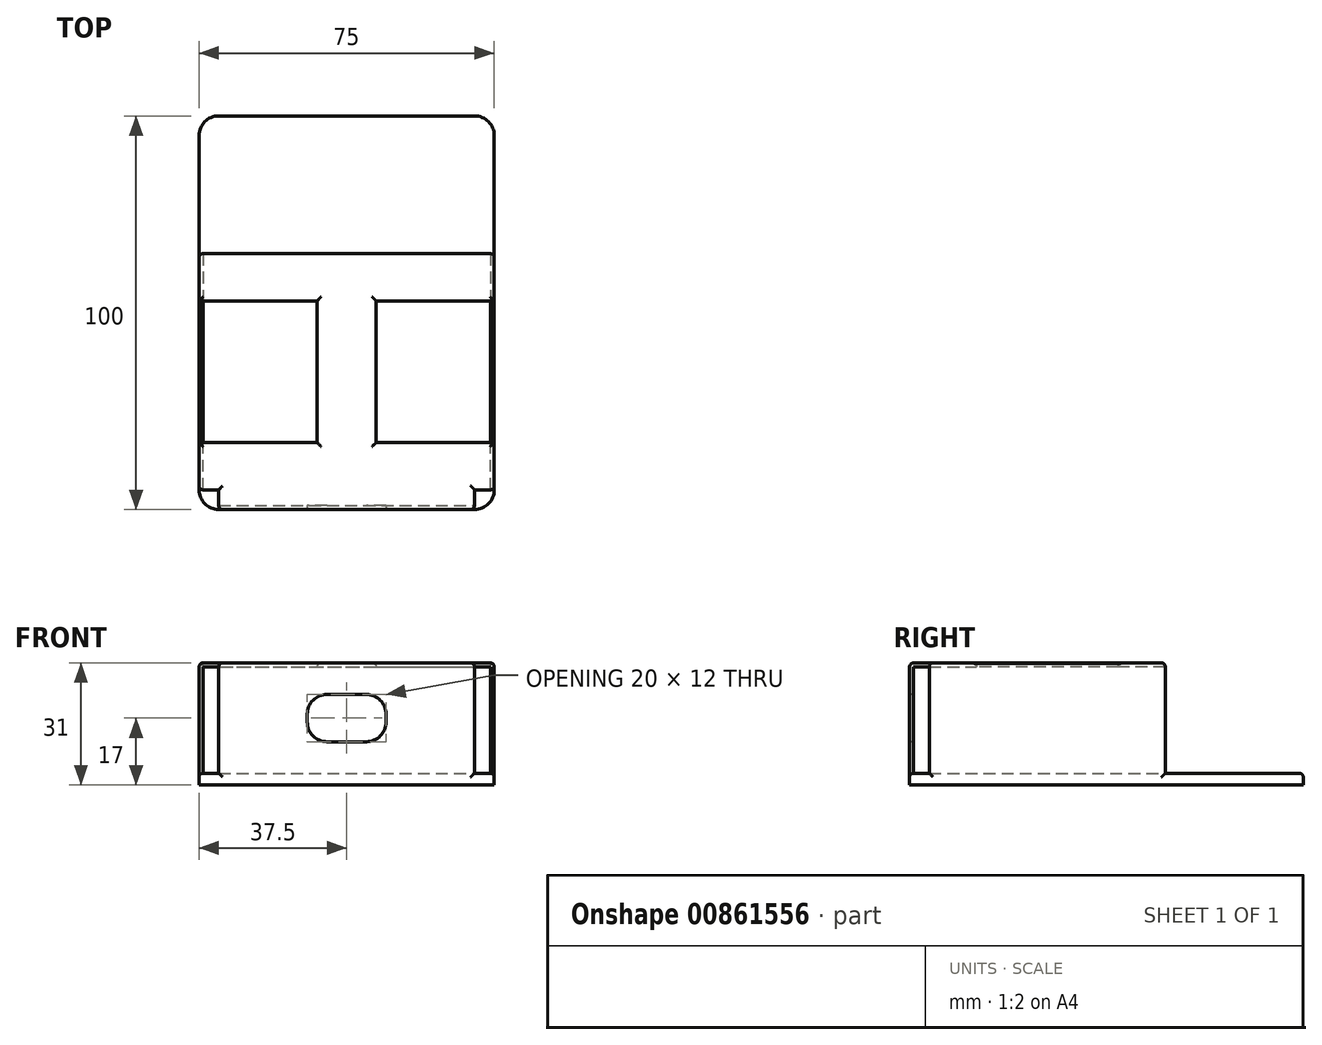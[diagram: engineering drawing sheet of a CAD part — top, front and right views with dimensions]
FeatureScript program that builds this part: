
annotation { "Feature Type Name" : "Feature", "Feature Type Description" : "" }
export const myFeature = defineFeature(function(context is Context, id is Id, definition is map)
    precondition{}
    {
        {
            var Q0;
            Q0=qCreatedBy(makeId("Top.planeOp"),FACE);
            var sketch = newSketch(context, id + "F0", { "sketchPlane" : qUnion([Q0])});
            skLineSegment(sketch, "E0.bottom", {"start": v(5, 0) * mm, "end": v(70, 0) * mm});
            skLineSegment(sketch, "E0.top", {"start": v(5, 100) * mm, "end": v(70, 100) * mm});
            skLineSegment(sketch, "E0.left", {"start": v(0, 5) * mm, "end": v(0, 95) * mm});
            skLineSegment(sketch, "E0.right", {"start": v(75, 5) * mm, "end": v(75, 95) * mm});
            skPoint(sketch, "E1.visualSharp", {"position": v(0, 100) * mm});
            skArc(sketch, "E1.filletArc", {"start": v(5, 100) * mm, "mid": v(1.46, 98.54) * mm, "end": v(0, 95) * mm});
            skPoint(sketch, "E2.visualSharp", {"position": v(75, 100) * mm});
            skArc(sketch, "E2.filletArc", {"start": v(75, 95) * mm, "mid": v(73.54, 98.54) * mm, "end": v(70, 100) * mm});
            skPoint(sketch, "E3.visualSharp", {"position": v(75, 0) * mm});
            skArc(sketch, "E3.filletArc", {"start": v(70, 0) * mm, "mid": v(73.54, 1.46) * mm, "end": v(75, 5) * mm});
            skPoint(sketch, "E4.visualSharp", {"position": v(0, 0) * mm});
            skArc(sketch, "E4.filletArc", {"start": v(0, 5) * mm, "mid": v(1.46, 1.46) * mm, "end": v(5, 0) * mm});
            skSolve(sketch);
        }
        {
            var Q0;
            Q0=makeQuery(id+"F0.imprint","IMPRINT",FACE,{"disambiguationData":[TD([[makeQuery(id+"F0.imprint","IMPRINT",EDGE,{"derivedFrom":sQuery(id+"F0.wireOp",EDGE,"E0.bottom")}),1.0]])]});
            extrude(context, id + "F1", {"entities" : qUnion([Q0]), "depth" : 3 * mm, "offsetDistance" : 25 * mm});
        }
        {
            var Q0;
            Q0=makeQuery(id+"F1.opExtrude","CAP_FACE",FACE,{"disambiguationData":[OSD([sQuery(id+"F0.wireOp",EDGE,"E0.bottom"),sQuery(id+"F0.wireOp",EDGE,"E0.top"),sQuery(id+"F0.wireOp",EDGE,"E0.left"),sQuery(id+"F0.wireOp",EDGE,"E0.right"),sQuery(id+"F0.wireOp",EDGE,"E1.filletArc"),sQuery(id+"F0.wireOp",EDGE,"E2.filletArc"),sQuery(id+"F0.wireOp",EDGE,"E3.filletArc"),sQuery(id+"F0.wireOp",EDGE,"E4.filletArc")])],"isStart":false});
            var sketch = newSketch(context, id + "F2", { "sketchPlane" : qUnion([Q0])});
            skPoint(sketch, "E5.oppositeSnap0", {"position": v(77.54, 1) * mm});
            skLineSegment(sketch, "E5.bottom", {"start": v(5, 0) * mm, "end": v(70, 0) * mm});
            skLineSegment(sketch, "E5.top", {"start": v(5, 1) * mm, "end": v(70, 1) * mm});
            skLineSegment(sketch, "E5.left", {"start": v(5, 0) * mm, "end": v(5, 1) * mm});
            skLineSegment(sketch, "E5.right", {"start": v(70, 0) * mm, "end": v(70, 1) * mm});
            skPoint(sketch, "E6.oppositeSnap0", {"position": v(1.46, 1.46) * mm});
            skLineSegment(sketch, "E7.bottom", {"start": v(0, 5) * mm, "end": v(1, 5) * mm});
            skLineSegment(sketch, "E7.top", {"start": v(0, 65) * mm, "end": v(1, 65) * mm});
            skLineSegment(sketch, "E7.left", {"start": v(0, 5) * mm, "end": v(0, 65) * mm});
            skLineSegment(sketch, "E7.right", {"start": v(1, 5) * mm, "end": v(1, 65) * mm});
            skLineSegment(sketch, "E8.bottom", {"start": v(75, 5) * mm, "end": v(74, 5) * mm});
            skLineSegment(sketch, "E8.top", {"start": v(75, 65) * mm, "end": v(74, 65) * mm});
            skLineSegment(sketch, "E8.left", {"start": v(75, 5) * mm, "end": v(75, 65) * mm});
            skLineSegment(sketch, "E8.right", {"start": v(74, 5) * mm, "end": v(74, 65) * mm});
            skSolve(sketch);
        }
        {
            var Q0;
            Q0=makeQuery(id+"F2.imprint","IMPRINT",FACE,{"disambiguationData":[TD([[makeQuery(id+"F2.imprint","IMPRINT",EDGE,{"derivedFrom":sQuery(id+"F2.wireOp",EDGE,"E7.bottom")}),1.0]])]});
            var Q1;
            Q1=makeQuery(id+"F2.imprint","IMPRINT",FACE,{"disambiguationData":[TD([[makeQuery(id+"F2.imprint","IMPRINT",EDGE,{"derivedFrom":sQuery(id+"F2.wireOp",EDGE,"E5.bottom")}),1.0]])]});
            var Q2;
            Q2=makeQuery(id+"F2.imprint","IMPRINT",FACE,{"disambiguationData":[TD([[makeQuery(id+"F2.imprint","IMPRINT",EDGE,{"derivedFrom":sQuery(id+"F2.wireOp",EDGE,"E8.bottom")}),-1.0]])]});
            var Q3;
            Q3 = qSketchRegion(id + "F10", true);
            extrude(context, id + "F3", {"entities" : qUnion([Q0, Q1, Q2, Q3]), "operationType" : NewBodyOperationType.ADD, "depth" : 28 * mm, "offsetDistance" : 25 * mm});
        }
        {
            var Q0;
            Q0=makeQuery(id+"F3.opExtrude","SWEPT_FACE",FACE,{"disambiguationData":[OSD([sQuery(id+"F2.wireOp",EDGE,"E8.right")])]});
            var sketch = newSketch(context, id + "F4", { "sketchPlane" : qUnion([Q0])});
            skLineSegment(sketch, "E9.bottom", {"start": v(-5, 31) * mm, "end": v(-17, 31) * mm});
            skLineSegment(sketch, "E9.top", {"start": v(-5, 30) * mm, "end": v(-17, 30) * mm});
            skLineSegment(sketch, "E9.left", {"start": v(-5, 31) * mm, "end": v(-5, 30) * mm});
            skLineSegment(sketch, "E9.right", {"start": v(-17, 31) * mm, "end": v(-17, 30) * mm});
            skLineSegment(sketch, "E10.bottom", {"start": v(-65, 31) * mm, "end": v(-53, 31) * mm});
            skLineSegment(sketch, "E10.top", {"start": v(-65, 30) * mm, "end": v(-53, 30) * mm});
            skLineSegment(sketch, "E10.left", {"start": v(-65, 31) * mm, "end": v(-65, 30) * mm});
            skLineSegment(sketch, "E10.right", {"start": v(-53, 31) * mm, "end": v(-53, 30) * mm});
            skSolve(sketch);
        }
        {
            var Q0;
            Q0=qSketchRegion(id+"F4",true);
            extrude(context, id + "F5", {"entities" : qUnion([Q0]), "operationType" : NewBodyOperationType.ADD, "endBound" : BoundingType.UP_TO_NEXT, "depth" : 25 * mm, "offsetDistance" : 25 * mm});
        }
        {
            var Q0;
            Q0=makeQuery(id+"F3.opExtrude","SWEPT_FACE",FACE,{"disambiguationData":[OSD([sQuery(id+"F2.wireOp",EDGE,"E5.top")])]});
            var sketch = newSketch(context, id + "F6", { "sketchPlane" : qUnion([Q0])});
            skLineSegment(sketch, "E11.bottom", {"start": v(-5, 31) * mm, "end": v(-70, 31) * mm});
            skLineSegment(sketch, "E11.top", {"start": v(-5, 30) * mm, "end": v(-70, 30) * mm});
            skLineSegment(sketch, "E11.left", {"start": v(-5, 31) * mm, "end": v(-5, 30) * mm});
            skLineSegment(sketch, "E11.right", {"start": v(-70, 31) * mm, "end": v(-70, 30) * mm});
            skSolve(sketch);
        }
        {
            var Q0;
            Q0=qSketchRegion(id+"F6",true);
            extrude(context, id + "F7", {"entities" : qUnion([Q0]), "operationType" : NewBodyOperationType.ADD, "endBound" : BoundingType.UP_TO_NEXT, "depth" : 25 * mm, "offsetDistance" : 25 * mm});
        }
        {
            var Q0;
            Q0=makeQuery(id+"F5.opExtrude","SWEPT_FACE",FACE,{"disambiguationData":[OSD([sQuery(id+"F4.wireOp",EDGE,"E9.right")])]});
            var sketch = newSketch(context, id + "F8", { "sketchPlane" : qUnion([Q0])});
            skLineSegment(sketch, "E12.bottom", {"start": v(-30, 31) * mm, "end": v(-45, 31) * mm});
            skLineSegment(sketch, "E12.top", {"start": v(-30, 30) * mm, "end": v(-45, 30) * mm});
            skLineSegment(sketch, "E12.left", {"start": v(-30, 31) * mm, "end": v(-30, 30) * mm});
            skLineSegment(sketch, "E12.right", {"start": v(-45, 31) * mm, "end": v(-45, 30) * mm});
            skPoint(sketch, "E13", {"position": v(-37.5, 31) * mm});
            skSolve(sketch);
        }
        {
            var Q0;
            Q0=qSketchRegion(id+"F8",true);
            extrude(context, id + "F9", {"entities" : qUnion([Q0]), "operationType" : NewBodyOperationType.ADD, "endBound" : BoundingType.UP_TO_NEXT, "depth" : 25 * mm, "offsetDistance" : 25 * mm});
        }
        {
            var Q0;
            Q0=makeQuery(id+"F3.boolean.opBoolean","MERGE",FACE,{"derivedFrom":[makeQuery(id+"F1.opExtrude","SWEPT_FACE",FACE,{"disambiguationData":[OSD([sQuery(id+"F0.wireOp",EDGE,"E0.bottom")])]}),makeQuery(id+"F3.opExtrude","SWEPT_FACE",FACE,{"disambiguationData":[OSD([sQuery(id+"F2.wireOp",EDGE,"E5.bottom")])]})]});
            var sketch = newSketch(context, id + "F10", { "sketchPlane" : qUnion([Q0])});
            skLineSegment(sketch, "E14.bottom", {"start": v(42.5, 23) * mm, "end": v(32.5, 23) * mm});
            skLineSegment(sketch, "E14.top", {"start": v(42.5, 11) * mm, "end": v(32.5, 11) * mm});
            skLineSegment(sketch, "E14.left", {"start": v(47.5, 18) * mm, "end": v(47.5, 16) * mm});
            skLineSegment(sketch, "E14.right", {"start": v(27.5, 18) * mm, "end": v(27.5, 16) * mm});
            skLineSegment(sketch, "E15", {"start": v(47.5, 17) * mm, "end": v(70, 17) * mm, "construction": true});
            skLineSegment(sketch, "E16", {"start": v(27.5, 17) * mm, "end": v(5, 17) * mm, "construction": true});
            skPoint(sketch, "E17.visualSharp", {"position": v(47.5, 23) * mm});
            skArc(sketch, "E17.filletArc", {"start": v(47.5, 18) * mm, "mid": v(46.04, 21.54) * mm, "end": v(42.5, 23) * mm});
            skPoint(sketch, "E18.visualSharp", {"position": v(47.5, 11) * mm});
            skArc(sketch, "E18.filletArc", {"start": v(42.5, 11) * mm, "mid": v(46.04, 12.46) * mm, "end": v(47.5, 16) * mm});
            skPoint(sketch, "E19.visualSharp", {"position": v(27.5, 11) * mm});
            skArc(sketch, "E19.filletArc", {"start": v(27.5, 16) * mm, "mid": v(28.96, 12.46) * mm, "end": v(32.5, 11) * mm});
            skPoint(sketch, "E20.visualSharp", {"position": v(27.5, 23) * mm});
            skArc(sketch, "E20.filletArc", {"start": v(32.5, 23) * mm, "mid": v(28.96, 21.54) * mm, "end": v(27.5, 18) * mm});
            skSolve(sketch);
        }
        {
            var Q0;
            Q0=makeQuery(id+"F10.imprint","IMPRINT",FACE,{"disambiguationData":[TD([[makeQuery(id+"F10.imprint","IMPRINT",EDGE,{"derivedFrom":sQuery(id+"F10.wireOp",EDGE,"E14.bottom")}),1.0]])]});
            extrude(context, id + "F11", {"entities" : qUnion([Q0]), "operationType" : NewBodyOperationType.REMOVE, "oppositeDirection" : true, "depth" : 25 * mm, "offsetDistance" : 25 * mm});
        }
        {
            var Q0;
            Q0=makeQuery(id+"F3.opExtrude","CAP_EDGE",EDGE,{"disambiguationData":[OSD([sQuery(id+"F2.wireOp",EDGE,"E8.left")])],"isStart":false});
            var Q1;
            Q1=makeQuery(id+"F3.opExtrude","CAP_EDGE",EDGE,{"disambiguationData":[OSD([sQuery(id+"F2.wireOp",EDGE,"E7.left")])],"isStart":false});
            var Q2;
            Q2=makeQuery(id+"F5.boolean.opBoolean","MERGE",EDGE,{"derivedFrom":[makeQuery(id+"F3.opExtrude","CAP_EDGE",EDGE,{"disambiguationData":[OSD([sQuery(id+"F2.wireOp",EDGE,"E7.top")])],"isStart":false}),makeQuery(id+"F3.opExtrude","CAP_EDGE",EDGE,{"disambiguationData":[OSD([sQuery(id+"F2.wireOp",EDGE,"E8.top")])],"isStart":false}),makeQuery(id+"F5.opExtrude","SWEPT_EDGE",EDGE,{"disambiguationData":[OSD([sQuery(id+"F4.wireOp",EDGE,"E10.bottom"),sQuery(id+"F4.wireOp",EDGE,"E10.left")])]})]});
            var Q3;
            Q3=makeQuery(id+"F3.opExtrude","SWEPT_EDGE",EDGE,{"disambiguationData":[OSD([sQuery(id+"F0.wireOp",EDGE,"E0.right"),sQuery(id+"F2.wireOp",EDGE,"E8.top"),sQuery(id+"F2.wireOp",EDGE,"E8.left")])]});
            var Q4;
            Q4=makeQuery(id+"F3.opExtrude","SWEPT_EDGE",EDGE,{"disambiguationData":[OSD([sQuery(id+"F0.wireOp",EDGE,"E0.left"),sQuery(id+"F2.wireOp",EDGE,"E7.top"),sQuery(id+"F2.wireOp",EDGE,"E7.left")])]});
            var Q5;
            Q5=makeQuery(id+"F1.opExtrude","CAP_EDGE",EDGE,{"disambiguationData":[OSD([sQuery(id+"F0.wireOp",EDGE,"E0.top")])],"isStart":false});
            var Q6;
            Q6=makeQuery(id+"F9.opExtrude","SWEPT_EDGE",EDGE,{"disambiguationData":[OSD([sQuery(id+"F2.wireOp",EDGE,"E8.right"),sQuery(id+"F4.wireOp",EDGE,"E9.bottom"),sQuery(id+"F4.wireOp",EDGE,"E9.right"),sQuery(id+"F8.wireOp",EDGE,"E12.bottom"),sQuery(id+"F8.wireOp",EDGE,"E12.left")])]});
            var Q7;
            {var subQ0=sQuery(id+"F2.wireOp",EDGE,"E8.right");var subQ1=sQuery(id+"F4.wireOp",EDGE,"E10.right");var subQ2=sQuery(id+"F2.wireOp",EDGE,"E7.right");var subQ3=sQuery(id+"F4.wireOp",EDGE,"E10.bottom");Q7=makeQuery(id+"F9.boolean.opBoolean","SPLIT",EDGE,{"disambiguationData":[TD([makeQuery(id+"F3.opExtrude","SWEPT_FACE",FACE,{"disambiguationData":[OSD([subQ2])]})])],"derivedFrom":makeQuery(id+"F5.opExtrude","SWEPT_EDGE",EDGE,{"disambiguationData":[OSD([subQ0,subQ3,subQ1])]})});}
            var Q8;
            Q8=makeQuery(id+"F9.opExtrude","SWEPT_EDGE",EDGE,{"disambiguationData":[OSD([sQuery(id+"F2.wireOp",EDGE,"E8.right"),sQuery(id+"F4.wireOp",EDGE,"E9.bottom"),sQuery(id+"F4.wireOp",EDGE,"E9.right"),sQuery(id+"F8.wireOp",EDGE,"E12.bottom"),sQuery(id+"F8.wireOp",EDGE,"E12.right")])]});
            var Q9;
            {var subQ0=sQuery(id+"F2.wireOp",EDGE,"E8.right");var subQ1=sQuery(id+"F4.wireOp",EDGE,"E10.right");var subQ2=sQuery(id+"F4.wireOp",EDGE,"E10.bottom");Q9=makeQuery(id+"F9.boolean.opBoolean","SPLIT",EDGE,{"disambiguationData":[TD([makeQuery(id+"F3.opExtrude","SWEPT_FACE",FACE,{"disambiguationData":[OSD([subQ0])]})])],"derivedFrom":makeQuery(id+"F5.opExtrude","SWEPT_EDGE",EDGE,{"disambiguationData":[OSD([subQ0,subQ2,subQ1])]})});}
            var Q10;
            {var subQ0=sQuery(id+"F2.wireOp",EDGE,"E8.right");var subQ1=sQuery(id+"F4.wireOp",EDGE,"E9.bottom");var subQ2=sQuery(id+"F4.wireOp",EDGE,"E9.right");Q10=makeQuery(id+"F9.boolean.opBoolean","SPLIT",EDGE,{"disambiguationData":[TD([makeQuery(id+"F3.opExtrude","SWEPT_FACE",FACE,{"disambiguationData":[OSD([subQ0])]})])],"derivedFrom":makeQuery(id+"F5.opExtrude","SWEPT_EDGE",EDGE,{"disambiguationData":[OSD([subQ0,subQ1,subQ2])]})});}
            var Q11;
            {var subQ0=sQuery(id+"F2.wireOp",EDGE,"E8.right");var subQ1=sQuery(id+"F2.wireOp",EDGE,"E7.right");var subQ2=sQuery(id+"F4.wireOp",EDGE,"E9.bottom");var subQ3=sQuery(id+"F4.wireOp",EDGE,"E9.right");Q11=makeQuery(id+"F9.boolean.opBoolean","SPLIT",EDGE,{"disambiguationData":[TD([makeQuery(id+"F3.opExtrude","SWEPT_FACE",FACE,{"disambiguationData":[OSD([subQ1])]})])],"derivedFrom":makeQuery(id+"F5.opExtrude","SWEPT_EDGE",EDGE,{"disambiguationData":[OSD([subQ0,subQ2,subQ3])]})});}
            var Q12;
            Q12=makeQuery(id+"F3.opExtrude","CAP_EDGE",EDGE,{"disambiguationData":[OSD([sQuery(id+"F2.wireOp",EDGE,"E8.right")])],"isStart":false});
            var Q13;
            Q13=makeQuery(id+"F3.opExtrude","CAP_EDGE",EDGE,{"disambiguationData":[OSD([sQuery(id+"F2.wireOp",EDGE,"E7.right")])],"isStart":false});
            var Q14;
            {var subQ1=sQuery(id+"F2.wireOp",EDGE,"E8.bottom");var subQ2=sQuery(id+"F2.wireOp",EDGE,"E7.right");var subQ3=sQuery(id+"F2.wireOp",EDGE,"E7.bottom");Q14=makeQuery(id+"F7.boolean.opBoolean","SPLIT",EDGE,{"disambiguationData":[TD([makeQuery(id+"F1.opExtrude","SWEPT_FACE",FACE,{"disambiguationData":[OSD([sQuery(id+"F0.wireOp",EDGE,"E0.right")])]})])],"derivedFrom":makeQuery(id+"F5.boolean.opBoolean","MERGE",EDGE,{"derivedFrom":[makeQuery(id+"F3.opExtrude","CAP_EDGE",EDGE,{"disambiguationData":[OSD([subQ3])],"isStart":false}),makeQuery(id+"F3.opExtrude","CAP_EDGE",EDGE,{"disambiguationData":[OSD([subQ1])],"isStart":false}),makeQuery(id+"F5.opExtrude","SWEPT_EDGE",EDGE,{"disambiguationData":[OSD([subQ3,subQ2])]})]})});}
            var Q15;
            Q15=makeQuery(id+"F7.boolean.opBoolean","MERGE",EDGE,{"derivedFrom":[makeQuery(id+"F3.opExtrude","CAP_EDGE",EDGE,{"disambiguationData":[OSD([sQuery(id+"F2.wireOp",EDGE,"E5.right")])],"isStart":false}),makeQuery(id+"F7.opExtrude","SWEPT_EDGE",EDGE,{"disambiguationData":[OSD([sQuery(id+"F6.wireOp",EDGE,"E11.bottom"),sQuery(id+"F6.wireOp",EDGE,"E11.right")])]})]});
            var Q16;
            Q16=makeQuery(id+"F7.boolean.opBoolean","MERGE",EDGE,{"derivedFrom":[makeQuery(id+"F3.opExtrude","CAP_EDGE",EDGE,{"disambiguationData":[OSD([sQuery(id+"F2.wireOp",EDGE,"E5.left")])],"isStart":false}),makeQuery(id+"F7.opExtrude","SWEPT_EDGE",EDGE,{"disambiguationData":[OSD([sQuery(id+"F6.wireOp",EDGE,"E11.bottom"),sQuery(id+"F6.wireOp",EDGE,"E11.left")])]})]});
            var Q17;
            {var subQ0=sQuery(id+"F2.wireOp",EDGE,"E8.bottom");var subQ2=sQuery(id+"F2.wireOp",EDGE,"E7.right");var subQ3=sQuery(id+"F2.wireOp",EDGE,"E7.bottom");Q17=makeQuery(id+"F7.boolean.opBoolean","SPLIT",EDGE,{"disambiguationData":[TD([makeQuery(id+"F1.opExtrude","SWEPT_FACE",FACE,{"disambiguationData":[OSD([sQuery(id+"F0.wireOp",EDGE,"E0.left")])]})])],"derivedFrom":makeQuery(id+"F5.boolean.opBoolean","MERGE",EDGE,{"derivedFrom":[makeQuery(id+"F3.opExtrude","CAP_EDGE",EDGE,{"disambiguationData":[OSD([subQ3])],"isStart":false}),makeQuery(id+"F3.opExtrude","CAP_EDGE",EDGE,{"disambiguationData":[OSD([subQ0])],"isStart":false}),makeQuery(id+"F5.opExtrude","SWEPT_EDGE",EDGE,{"disambiguationData":[OSD([subQ3,subQ2])]})]})});}
            var Q18;
            Q18=makeQuery(id+"F3.opExtrude","CAP_EDGE",EDGE,{"disambiguationData":[OSD([sQuery(id+"F2.wireOp",EDGE,"E5.bottom")])],"isStart":false});
            var Q19;
            Q19=makeQuery(id+"F11.boolean.opBoolean","COPY",EDGE,{"derivedFrom":makeQuery(id+"F11.opExtrude","CAP_EDGE",EDGE,{"disambiguationData":[OSD([sQuery(id+"F10.wireOp",EDGE,"E14.bottom")])],"isStart":true})});
            var Q20;
            Q20=makeQuery(id+"F11.boolean.opBoolean","COPY",EDGE,{"derivedFrom":makeQuery(id+"F11.opExtrude","CAP_EDGE",EDGE,{"disambiguationData":[OSD([sQuery(id+"F10.wireOp",EDGE,"E17.filletArc")])],"isStart":true})});
            var Q21;
            Q21=makeQuery(id+"F3.opExtrude","SWEPT_EDGE",EDGE,{"disambiguationData":[OSD([sQuery(id+"F0.wireOp",EDGE,"E4.filletArc"),sQuery(id+"F2.wireOp",EDGE,"E5.bottom"),sQuery(id+"F2.wireOp",EDGE,"E5.left")])]});
            var Q22;
            Q22=makeQuery(id+"F3.opExtrude","SWEPT_EDGE",EDGE,{"disambiguationData":[OSD([sQuery(id+"F0.wireOp",EDGE,"E4.filletArc"),sQuery(id+"F2.wireOp",EDGE,"E7.bottom"),sQuery(id+"F2.wireOp",EDGE,"E7.left")])]});
            var Q23;
            Q23=makeQuery(id+"F1.opExtrude","CAP_EDGE",EDGE,{"disambiguationData":[OSD([sQuery(id+"F0.wireOp",EDGE,"E4.filletArc")])],"isStart":false});
            var Q24;
            Q24=makeQuery(id+"F3.opExtrude","SWEPT_EDGE",EDGE,{"disambiguationData":[OSD([sQuery(id+"F0.wireOp",EDGE,"E3.filletArc"),sQuery(id+"F2.wireOp",EDGE,"E5.bottom"),sQuery(id+"F2.wireOp",EDGE,"E5.right")])]});
            var Q25;
            Q25=makeQuery(id+"F3.opExtrude","SWEPT_EDGE",EDGE,{"disambiguationData":[OSD([sQuery(id+"F0.wireOp",EDGE,"E3.filletArc"),sQuery(id+"F2.wireOp",EDGE,"E8.bottom"),sQuery(id+"F2.wireOp",EDGE,"E8.left")])]});
            var Q26;
            Q26=makeQuery(id+"F1.opExtrude","CAP_EDGE",EDGE,{"disambiguationData":[OSD([sQuery(id+"F0.wireOp",EDGE,"E3.filletArc")])],"isStart":false});
            fillet(context, id + "F12", {"entities" : qUnion([Q0, Q1, Q2, Q3, Q4, Q5, Q6, Q7, Q8, Q9, Q10, Q11, Q12, Q13, Q14, Q15, Q16, Q17, Q18, Q19, Q20, Q21, Q22, Q23, Q24, Q25, Q26]), "radius" : 1 * mm, "tangentPropagation" : true, "allowEdgeOverflow" : false});
        }
    });
